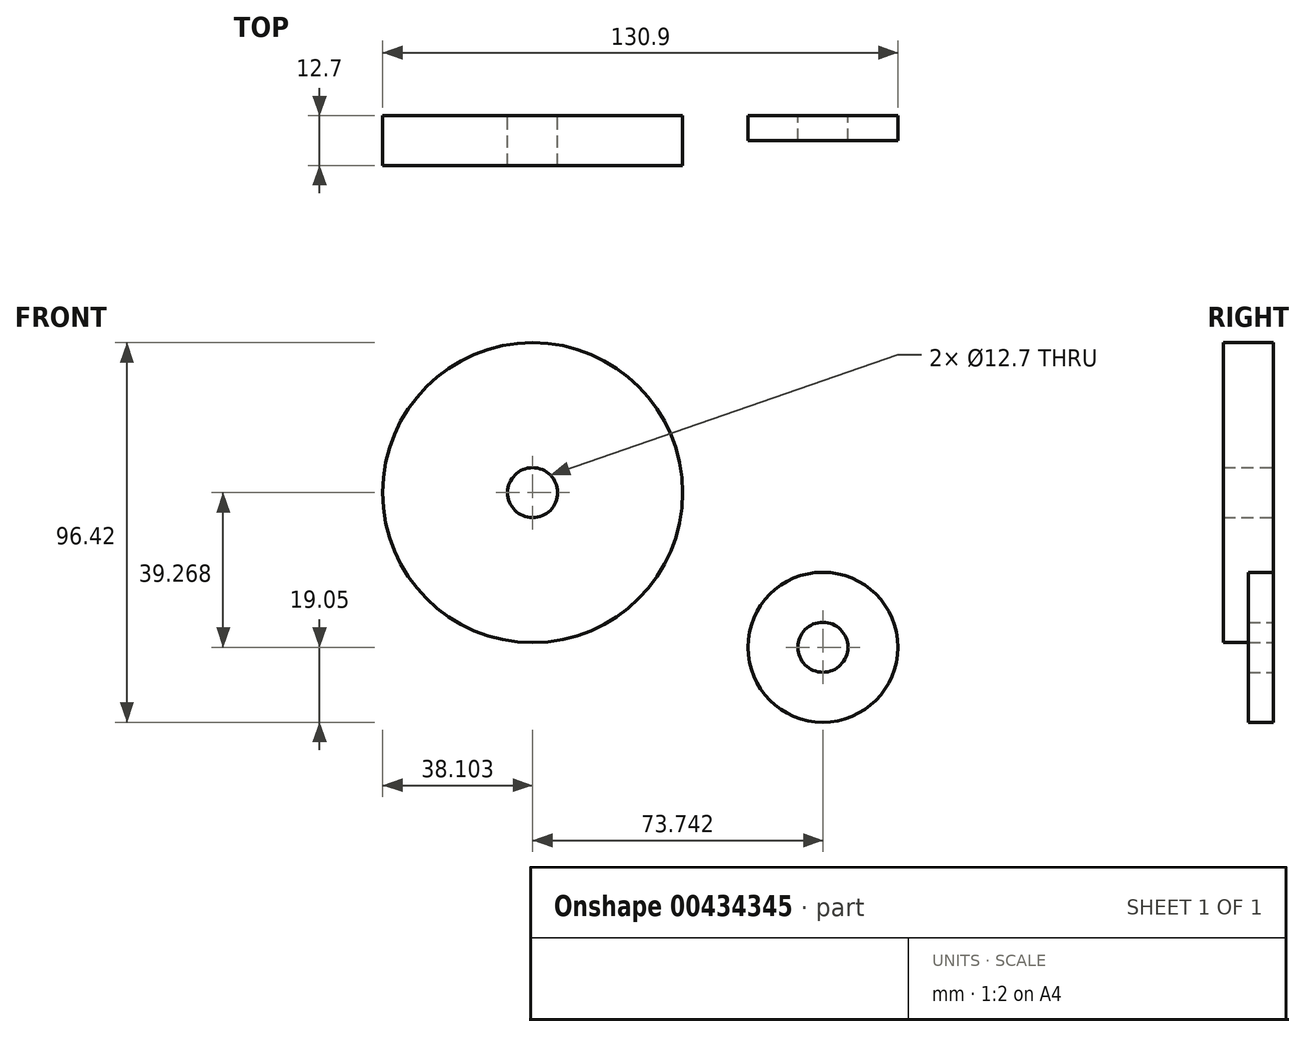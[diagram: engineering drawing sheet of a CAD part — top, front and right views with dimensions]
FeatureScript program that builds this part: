
annotation { "Feature Type Name" : "Feature", "Feature Type Description" : "" }
export const myFeature = defineFeature(function(context is Context, id is Id, definition is map)
    precondition{}
    {
        {
            var Q0;
            Q0=qCreatedBy(makeId("Front.planeOp"),FACE);
            var sketch = newSketch(context, id + "F0", { "sketchPlane" : qUnion([Q0])});
            skCircle(sketch, "E0", {"center": v(-36.69, 19.36) * mm, "radius": 6.35 * mm});
            skCircle(sketch, "E1", {"center": v(-36.69, 19.36) * mm, "radius": 38.1 * mm});
            skSolve(sketch);
        }
        {
            var Q0;
            Q0=makeQuery(id+"F0.imprint","IMPRINT",FACE,{"disambiguationData":[TD([[makeQuery(id+"F0.imprint","IMPRINT",EDGE,{"derivedFrom":sQuery(id+"F0.wireOp",EDGE,"E0")}),-1.0]])]});
            extrude(context, id + "F1", {"entities" : qUnion([Q0]), "depth" : 12.7 * mm});
        }
        {
            var Q0;
            Q0=qCreatedBy(makeId("Front.planeOp"),FACE);
            var sketch = newSketch(context, id + "F2", { "sketchPlane" : qUnion([Q0])});
            skCircle(sketch, "E2", {"center": v(37.06, -19.91) * mm, "radius": 19.05 * mm});
            skCircle(sketch, "E3", {"center": v(37.06, -19.91) * mm, "radius": 6.35 * mm});
            skPoint(sketch, "E4.visualSharp", {"position": v(18.27, -9.83) * mm});
            skSolve(sketch);
        }
        {
            var Q0;
            Q0=makeQuery(id+"F2.imprint","IMPRINT",FACE,{"disambiguationData":[TD([[makeQuery(id+"F2.imprint","IMPRINT",EDGE,{"derivedFrom":sQuery(id+"F2.wireOp",EDGE,"E2")}),1.0]])]});
            extrude(context, id + "F3", {"entities" : qUnion([Q0]), "depth" : 6.35 * mm});
        }
    });
